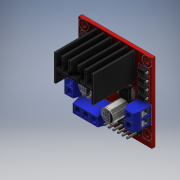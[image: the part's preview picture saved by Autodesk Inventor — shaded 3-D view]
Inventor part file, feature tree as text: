
AUTODESK INVENTOR PART (.ipt)
format: ipt  version: 2019 (Build 230136000, 136)  size: 2,064,896 bytes
history: native  units: mm
features: extrude x31, sketch x22, chamfer x13, fillet x7, pattern_linear x7, other x4, plane x4, projected_geometry x4, mirror x3
ambient origin geometry x8: Origin, YZ Plane, XZ Plane, XY Plane, X Axis, Y Axis, Z Axis, Center Point
bodies: Solid1 (feature_tree)
feature tree (95):
  extrude  "Extrusion1"  Depth=44.0mm
  extrude  "Extrusion2"  Depth=3.0mm
  fillet  "Fillet1"  Radius=2.5mm
  extrude  "Extrusion3"  Depth=6.0mm
  sketch  "Sketch4"  dims[d12=6.0mm d13=2.0mm d14=0.0mm]
  extrude  "Extrusion4"  Depth=2.0mm TaperAngle=0.0deg
  extrude  "Extrusion5"  Depth=23.5mm
  chamfer  "Chamfer1"  Distance=25.0mm
  sketch  "Sketch5"  dims[d15=2.0mm d16=23.5mm]
  extrude  "Extrusion6"  Depth=0.5mm
  extrude  "Extrusion7"  Depth=1.5mm
  chamfer  "Chamfer2"  Distance=20.0mm
  chamfer  "Chamfer3"  Distance=21.0mm
  chamfer  "Chamfer4"  Distance=15.0mm
  chamfer  "Chamfer5"  Distance=1.5mm Angle=45.0deg
  chamfer  "Chamfer6"  Distance=12.5mm
  chamfer  "Chamfer7"  Distance=10.0mm
  extrude  "Extrusion8"  Depth=7.5mm
  extrude  "Extrusion9"  Depth=0.5mm
  fillet  "Fillet2"  Radius=4.0mm
  sketch  "Sketch7"  dims[d17=1.0mm]
  extrude  "Extrusion10"  Depth=0.5mm
  extrude  "Extrusion11"  Depth=6.5mm
  fillet  "Fillet3"  Radius=15.0mm
  pattern_linear  "Rectangular Pattern1"  Spacing1=5.0mm  [1 undecoded]
  mirror  "Mirror1"
  sketch  "Sketch9"  dims[d18=16.0mm]
  other  "Decal2"
  other  "Decal3"
  chamfer  "Chamfer8"  Distance=5.0mm
  fillet  "Fillet5"  Radius=3.5mm
  extrude  "Extrusion12"  Depth=2.5mm
  sketch  "Sketch12"  dims[d20=1.0mm]
  extrude  "Extrusion13"  Depth=2.5mm
  fillet  "Fillet6"  Radius=2.5mm
  extrude  "Extrusion14"  Depth=2.5mm
  sketch  "Sketch13"  dims[d21=1.0mm]
  extrude  "Extrusion15"  Depth=2.5mm
  extrude  "Extrusion16"  Depth=2.5mm
  extrude  "Extrusion17"  Depth=4.4mm
  extrude  "Extrusion18"  Depth=0.6mm
  fillet  "Fillet7"  Radius=10.0mm
  chamfer  "Chamfer9"  Distance=15.0mm
  extrude  "Extrusion19"  Depth=3.5mm TaperAngle=15.0deg
  plane  "Work Plane1"
  extrude  "Extrusion20"  Depth=3.5mm TaperAngle=15.0deg
  pattern_linear  "Rectangular Pattern2"  Spacing1=3.5mm  [1 undecoded]
  plane  "Work Plane2"
  extrude  "Extrusion21"  Depth=4.0mm
  pattern_linear  "Rectangular Pattern3"  Spacing1=4.0mm  [1 undecoded]
  extrude  "Extrusion22"  Depth=4.0mm
  fillet  "Fillet8"  Radius=8.0mm
  extrude  "Extrusion23"  Depth=6.5mm
  pattern_linear  "Rectangular Pattern4"  Spacing1=3.0mm  [1 undecoded]
  extrude  "Extrusion24"  Depth=6.5mm
  pattern_linear  "Rectangular Pattern5"  Spacing1=8.0mm  [1 undecoded]
  sketch  "Sketch19"  dims[d27=3.3mm]
  mirror  "Mirror2"
  extrude  "Extrusion25"  Depth=8.0mm
  plane  "Work Plane3"
  sketch  "Sketch21"  dims[d29=3.3mm]
  extrude  "Extrusion27"  Depth=11.0mm TaperAngle=0.0deg
  extrude  "Extrusion28"  Depth=1.0mm TaperAngle=0.0deg
  chamfer  "Chamfer10"  Distance=0.5mm
  chamfer  "Chamfer11"  Distance=4.0mm
  pattern_linear  "Rectangular Pattern6"  Spacing1=2.5mm  [1 undecoded]
  sketch  "Sketch22"  dims[d30=3.3mm d31=25.0mm d32=0.0mm]
  extrude  "Extrusion29"  Depth=7.0mm
  plane  "Work Plane4"
  sketch  "Sketch24"  dims[d35=0.0mm d36=1.5mm]
  extrude  "Extrusion30"  Depth=2.5mm
  extrude  "Extrusion31"  Depth=1.0mm
  chamfer  "Chamfer12"  Distance=0.5mm
  chamfer  "Chamfer13"  Distance=2.0mm
  pattern_linear  "Rectangular Pattern7"  Spacing1=1.5mm  [1 undecoded]
  mirror  "Mirror3"
  extrude  "Extrusion32"  Depth=0.5mm
  sketch  "Sketch1"  dims[d0=47.0mm d1=44.0mm]
  sketch  "Sketch2"  dims[d2=2.0mm d3=0.0mm d4=3.0mm d6=2.5mm]
  sketch  "Sketch3"  dims[d10=2.5mm d11=6.0mm]
  projected_geometry  "Projected Loop1"
  projected_geometry  "Projected Loop2"
  other  "Image2"
  other  "Image3"
  sketch  "Sketch10"  dims[d19=7.0mm]
  sketch  "Sketch14"  dims[d22=1.0mm]
  sketch  "Sketch15"  dims[d23=1.0mm]
  sketch  "Sketch16"  dims[d24=1.0mm]
  sketch  "Sketch17"  dims[d25=1.0mm]
  sketch  "Sketch18"  dims[d26=1.0mm]
  sketch  "Sketch20"  dims[d28=3.3mm]
  projected_geometry  "Projected Loop3"
  sketch  "Sketch23"  dims[d33=0.5mm d34=0.5mm]
  projected_geometry  "Projected Loop4"
  sketch  "Sketch25"  dims[d37=3.0mm d38=20.0mm d39=21.0mm d40=0.0mm d41=15.0mm d42=0.0mm d43=1.5mm d44=2.0mm d45=45.0deg d46=12.5mm d47=10.0mm d48=7.5mm d49=0.5mm d50=4.0mm d51=0.5mm d52=6.5mm d53=15.0mm d55=5.0mm d56=5.0mm d57=3.5mm d58=2.5mm d59=2.5mm d60=2.5mm d61=2.5mm d62=2.5mm d63=2.5mm d64=4.4mm d65=0.6mm d66=10.0mm d67=0.0mm d68=15.0mm d69=0.0mm d70=3.5mm d71=2.0mm d72=15.0deg d73=3.5mm d74=2.0mm d75=15.0deg d76=3.5mm d77=2.0mm d78=15.0deg d79=4.0mm d80=2.0mm d81=3.490659mm d82=4.0mm d83=2.0mm d84=3.490659mm d85=4.0mm d86=2.0mm d87=3.490659mm d88=8.0mm d89=6.5mm d90=3.0mm d91=6.5mm d92=8.0mm d93=8.0mm d94=11.0mm d95=0.0mm d96=1.0mm d97=0.0mm d98=0.5mm d99=4.0mm d100=2.5mm d101=7.0mm d102=2.5mm d103=1.0mm d104=0.5mm d105=2.0mm d106=0.0mm d107=1.5mm d108=0.0mm d109=0.5mm d111=40.0mm d113=4.5mm d184=2.0mm d185=2.0mm d186=45.0deg d187=0.5mm d188=3.0mm d189=6.0mm d190=10.0mm d191=0.0mm d201=2.5mm d202=0.25mm d203=0.5mm d204=60.0mm d206=2.75mm d207=10.0mm d209=10.0mm d211=0.25mm d212=1.0mm d213=1.0mm d214=2.5mm d215=0.0mm d216=0.5mm d217=0.85mm d218=0.85mm d219=8.0mm d220=0.0mm d221=6.0mm d222=0.0mm d223=1.0mm d224=0.5mm d225=0.5mm d226=1.5mm d227=0.25mm d228=0.25mm d229=3.0mm d230=0.75mm d231=1.0mm d232=0.75mm d233=2.0mm d234=0.0mm d235=0.5mm d236=0.0mm d237=1.0mm d238=0.0mm d239=0.25mm d240=0.0mm d241=1.0mm d242=0.5mm d243=2.0mm d244=45.0deg d245=10.0mm d246=1.5mm d247=0.5mm d248=0.5mm d249=0.25mm d250=0.0mm d251=6.5mm d252=1.0mm d253=1.0mm d254=0.5mm d255=1.0mm d256=1.0mm d257=1.0mm d258=0.25mm d259=0.6mm d260=1.0mm d261=1.5mm d262=0.7mm d263=0.0mm d264=80.0mm d266=2.7mm d267=6.5mm d268=1.0mm d269=0.5mm d270=1.0mm d271=1.0mm d272=0.5mm d273=1.0mm d274=0.7mm d275=0.0mm d276=70.0mm d278=2.7mm d279=1.0mm d280=1.0mm d281=0.5mm d282=0.5mm d283=1.0mm d284=1.0mm d285=0.5mm d286=1.0mm d287=1.0mm d288=0.5mm d289=0.0mm d290=0.5mm d291=4.0mm d293=5.0mm d296=1.0mm d297=6.0mm d298=0.0mm d299=30.0mm d301=5.0mm d305=5.0mm d306=4.0mm d307=0.75mm d308=1.0mm d309=6.0mm d310=0.0mm d311=20.0mm d313=5.0mm d314=0.75mm d315=0.1mm d316=0.1mm d317=0.1mm d318=0.1mm d319=0.5mm d321=0.4mm d322=5.25mm d323=0.0mm d324=0.25mm d325=5.5mm d326=0.25mm d327=17.453293mm d328=19.198622mm d329=3.5mm d330=2.0mm d331=0.5mm d334=2.5mm d335=0.0mm d336=3.8mm d337=0.0mm d338=1.5mm d339=0.65mm d340=45.0deg d341=1.5mm d342=0.65mm d343=45.0deg d344=30.0mm d346=5.0mm d347=0.1mm d348=0.1mm d349=0.1mm d350=0.1mm d351=0.5mm d352=0.4mm d353=5.25mm d354=0.0mm d355=5.5mm d356=2.0mm d357=0.25mm d358=0.25mm d359=19.198622mm d360=17.453293mm d361=3.5mm d362=0.5mm d363=2.5mm d364=0.0mm d365=3.8mm d366=0.0mm d367=1.5mm d368=0.65mm d369=45.0deg d370=1.5mm d371=0.65mm d372=45.0deg d373=20.0mm d375=5.0mm d378=38.0mm d379=38.0mm d380=5.5mm d381=0.25mm d382=0.25mm d383=0.25mm d384=0.25mm d385=3.0mm d386=0.15mm d387=0.01mm d388=0.0mm d389=0.15mm d390=0.25mm d391=0.15mm d392=0.25mm d393=0.15mm d394=0.25mm d395=7.5mm d396=0.5mm d397=0.5mm d398=0.25mm d399=3.5mm d401=6.5mm d402=135.0deg d403=2.5mm d404=0.25mm d405=40.0mm d407=4.5mm d408=10.0mm d410=10.0mm d412=1.5mm d413=1.5mm d414=4.0mm d415=7.0mm]
note: 7 required parameter values undecoded (feature->parameter linkage not recoverable at this tier; creation-order binding heuristic only, values carry confidence <= 0.55)
